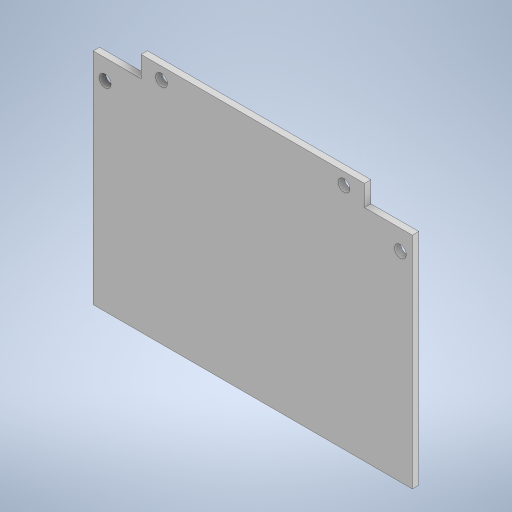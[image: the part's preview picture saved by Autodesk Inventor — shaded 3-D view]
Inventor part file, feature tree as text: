
AUTODESK INVENTOR PART (.ipt)
format: ipt  version: 2023 (Build 270158000, 158)  size: 292,864 bytes
history: native  units: in
note: dims shown in document units (in); Inventor stores cm internally (conversion verified against a paired STEP export)
features: reference x16, other x6, extrude x6, sketch x6, projected_geometry x5
ambient origin geometry x8: Origin, YZ Plane, XZ Plane, XY Plane, X Axis, Y Axis, Z Axis, Center Point
bodies: Body1 (feature_tree)
feature tree (39):
  other  "Bryła1"
  extrude  "Wyciągnięcie proste1"  Depth=0.0787in
  extrude  "Wyciągnięcie proste2"  Depth=0.0787in
  extrude  "Wyciągnięcie proste3"  Depth=0.0787in
  extrude  "Wyciągnięcie proste4"  Depth=0.0787in
  extrude  "Wyciągnięcie proste5"  Depth=0.063in TaperAngle=0.0deg
  extrude  "Wyciągnięcie proste6"  Depth=0.315in TaperAngle=0.0deg
  sketch  "Szkic1"
  reference  "Odniesienie1"
  reference  "Odniesienie2"
  reference  "Odniesienie3"
  reference  "Odniesienie4"
  reference  "Odniesienie5"
  reference  "Odniesienie6"
  reference  "Odniesienie7"
  reference  "Odniesienie8"
  reference  "Odniesienie9"
  reference  "Odniesienie10"
  reference  "Odniesienie11"
  reference  "Odniesienie12"
  reference  "Odniesienie13"
  reference  "Odniesienie14"
  reference  "Odniesienie15"
  reference  "Odniesienie16"
  sketch  "Szkic2"
  projected_geometry  "Pętla rzutowana1"
  sketch  "Szkic3"
  projected_geometry  "Pętla rzutowana2"
  sketch  "Szkic4"
  projected_geometry  "Pętla rzutowana3"
  sketch  "Szkic5"
  projected_geometry  "Pętla rzutowana4"
  sketch  "Szkic6"
  projected_geometry  "Pętla rzutowana5"
  other  "Zespół3"
  other  "uchwyt_na_silnik:1"
  other  "SCIANA_2.0_MIR:1"
  other  "SCIANA_2.0:1"
  other  "minisumopodsr:1"
